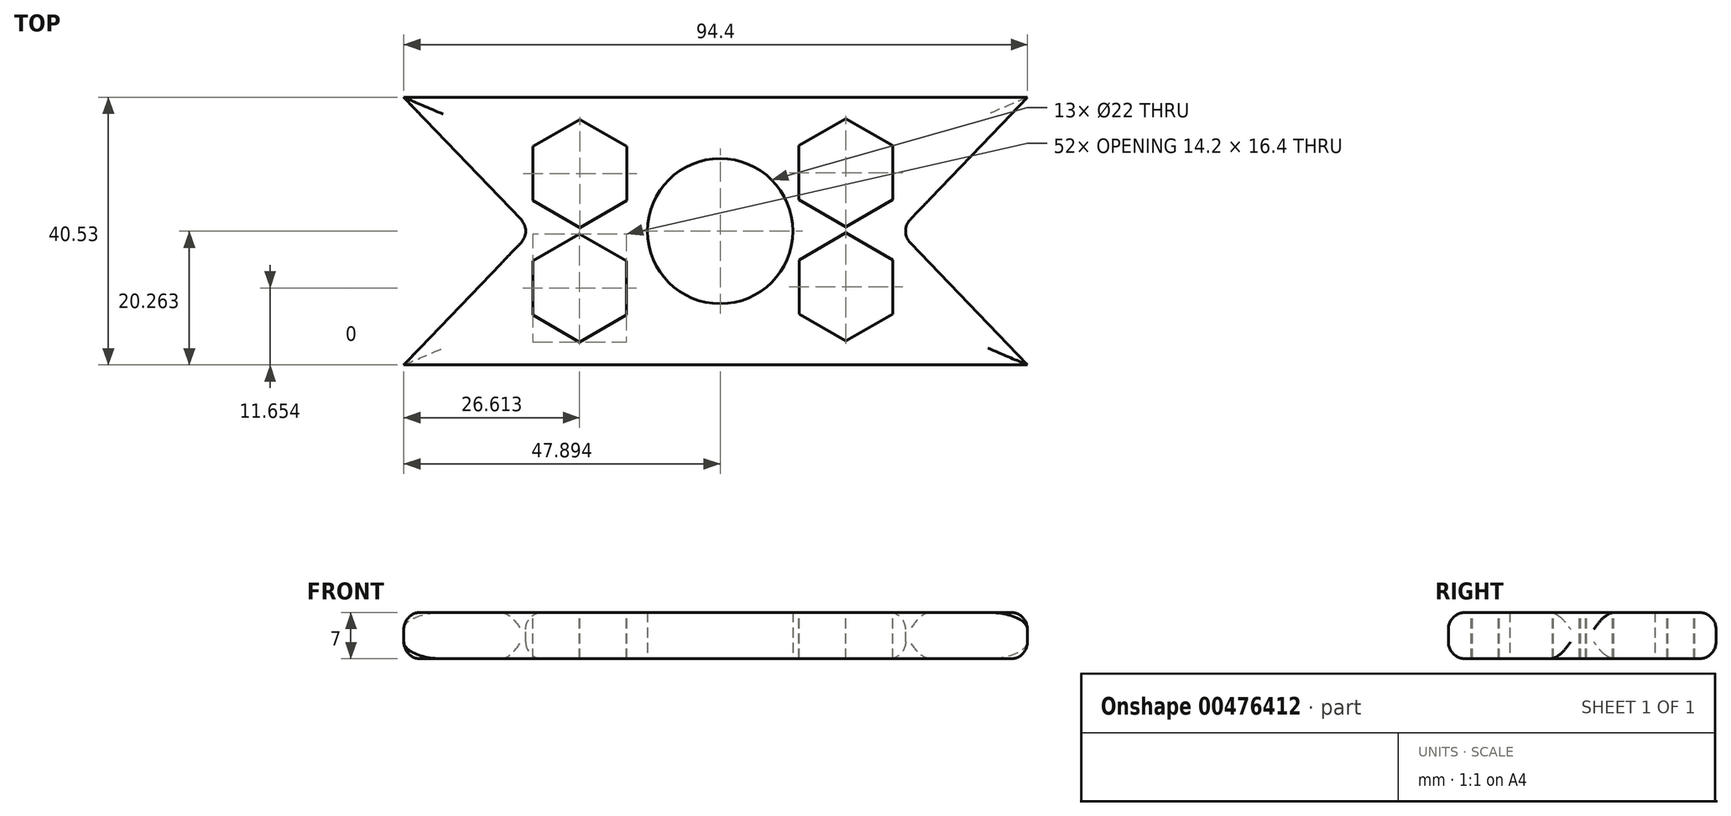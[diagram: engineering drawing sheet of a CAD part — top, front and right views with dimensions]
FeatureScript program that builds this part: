
annotation { "Feature Type Name" : "Feature", "Feature Type Description" : "" }
export const myFeature = defineFeature(function(context is Context, id is Id, definition is map)
    precondition{}
    {
        {
            var Q0;
            Q0=qCreatedBy(makeId("Top.planeOp"),FACE);
            var sketch = newSketch(context, id + "F0", { "sketchPlane" : qUnion([Q0])});
            skLineSegment(sketch, "E0", {"start": v(1.37, -16.47) * mm, "end": v(-46.52, -16.47) * mm});
            skLineSegment(sketch, "E1", {"start": v(-46.52, 24.06) * mm, "end": v(1.37, 24.06) * mm});
            skLineSegment(sketch, "E2", {"start": v(1.37, 24.06) * mm, "end": v(47.88, 24.06) * mm});
            skLineSegment(sketch, "E3", {"start": v(1.37, -16.47) * mm, "end": v(47.88, -16.47) * mm});
            skCircle(sketch, "E4", {"center": v(1.37, 3.8) * mm, "radius": 11 * mm});
            skLineSegment(sketch, "E5", {"start": v(-46.52, 24.06) * mm, "end": v(-27.1, 3.8) * mm});
            skLineSegment(sketch, "E6", {"start": v(-27.1, 3.8) * mm, "end": v(-46.52, -16.47) * mm});
            skLineSegment(sketch, "E7", {"start": v(47.88, 24.06) * mm, "end": v(28.47, 3.8) * mm});
            skLineSegment(sketch, "E8", {"start": v(28.47, 3.8) * mm, "end": v(47.88, -16.47) * mm});
            skArc(sketch, "E9", {"start": v(-36.8, 13.92) * mm, "mid": v(-38.9, 3.8) * mm, "end": v(-36.8, -6.34) * mm});
            skArc(sketch, "E10", {"start": v(38.18, -6.34) * mm, "mid": v(40.27, 3.8) * mm, "end": v(38.18, 13.92) * mm});
            skSolve(sketch);
        }
        {
            var Q0;
            Q0=makeQuery(id+"F0.imprint","IMPRINT",FACE,{"disambiguationData":[TD([[makeQuery(id+"F0.imprint","IMPRINT",EDGE,{"derivedFrom":sQuery(id+"F0.wireOp",EDGE,"E0")}),-1.0]])]});
            extrude(context, id + "F1", {"entities" : qUnion([Q0]), "depth" : 7 * mm});
        }
        {
            var Q0;
            Q0=makeQuery(id+"F1.opExtrude","CAP_EDGE",EDGE,{"disambiguationData":[OSD([sQuery(id+"F0.wireOp",EDGE,"E0"),sQuery(id+"F0.wireOp",EDGE,"E3")])],"isStart":false});
            var Q1;
            Q1=makeQuery(id+"F1.opExtrude","CAP_EDGE",EDGE,{"disambiguationData":[OSD([sQuery(id+"F0.wireOp",EDGE,"E1"),sQuery(id+"F0.wireOp",EDGE,"E2")])],"isStart":false});
            var Q2;
            Q2=makeQuery(id+"F1.opExtrude","CAP_EDGE",EDGE,{"disambiguationData":[OSD([sQuery(id+"F0.wireOp",EDGE,"E1"),sQuery(id+"F0.wireOp",EDGE,"E2")])],"isStart":true});
            var Q3;
            Q3=makeQuery(id+"F1.opExtrude","CAP_EDGE",EDGE,{"disambiguationData":[OSD([sQuery(id+"F0.wireOp",EDGE,"E0"),sQuery(id+"F0.wireOp",EDGE,"E3")])],"isStart":true});
            var Q4;
            Q4=makeQuery(id+"F1.opExtrude","SWEPT_EDGE",EDGE,{"disambiguationData":[OSD([sQuery(id+"F0.wireOp",EDGE,"E7"),sQuery(id+"F0.wireOp",EDGE,"E8")])]});
            var Q5;
            Q5=makeQuery(id+"F1.opExtrude","SWEPT_EDGE",EDGE,{"disambiguationData":[OSD([sQuery(id+"F0.wireOp",EDGE,"E5"),sQuery(id+"F0.wireOp",EDGE,"E6")])]});
            var Q6;
            Q6=makeQuery(id+"F1.opExtrude","CAP_EDGE",EDGE,{"disambiguationData":[OSD([sQuery(id+"F0.wireOp",EDGE,"E8")])],"isStart":false});
            var Q7;
            Q7=makeQuery(id+"F1.opExtrude","CAP_EDGE",EDGE,{"disambiguationData":[OSD([sQuery(id+"F0.wireOp",EDGE,"E5")])],"isStart":false});
            var Q8;
            Q8=makeQuery(id+"F1.opExtrude","CAP_EDGE",EDGE,{"disambiguationData":[OSD([sQuery(id+"F0.wireOp",EDGE,"E6")])],"isStart":true});
            var Q9;
            Q9=makeQuery(id+"F1.opExtrude","CAP_EDGE",EDGE,{"disambiguationData":[OSD([sQuery(id+"F0.wireOp",EDGE,"E7")])],"isStart":true});
            fillet(context, id + "F2", {"entities" : qUnion([Q0, Q1, Q2, Q3, Q4, Q5, Q6, Q7, Q8, Q9]), "radius" : 2.54 * mm, "tangentPropagation" : true, "allowEdgeOverflow" : false});
        }
        {
            var Q0;
            Q0=makeQuery(id+"F1.opExtrude","CAP_FACE",FACE,{"disambiguationData":[OSD([sQuery(id+"F0.wireOp",EDGE,"E0"),sQuery(id+"F0.wireOp",EDGE,"E1"),sQuery(id+"F0.wireOp",EDGE,"E2"),sQuery(id+"F0.wireOp",EDGE,"E3"),sQuery(id+"F0.wireOp",EDGE,"E4"),sQuery(id+"F0.wireOp",EDGE,"E5"),sQuery(id+"F0.wireOp",EDGE,"E6"),sQuery(id+"F0.wireOp",EDGE,"E7"),sQuery(id+"F0.wireOp",EDGE,"E8")])],"isStart":false});
            var sketch = newSketch(context, id + "F3", { "sketchPlane" : qUnion([Q0])});
            skPoint(sketch, "E11.0.midPoint", {"position": v(-8.39, 9.42) * mm});
            skLineSegment(sketch, "E12.0", {"start": v(-12.75, 16.6) * mm, "end": v(-12.75, 8.4) * mm});
            skLineSegment(sketch, "E12.1", {"start": v(-12.75, 8.4) * mm, "end": v(-19.85, 4.3) * mm});
            skLineSegment(sketch, "E12.2", {"start": v(-19.85, 4.3) * mm, "end": v(-26.95, 8.4) * mm});
            skLineSegment(sketch, "E12.3", {"start": v(-26.95, 8.4) * mm, "end": v(-26.95, 16.6) * mm});
            skLineSegment(sketch, "E12.4", {"start": v(-26.95, 16.6) * mm, "end": v(-19.85, 20.7) * mm});
            skLineSegment(sketch, "E12.5", {"start": v(-19.85, 20.7) * mm, "end": v(-12.75, 16.6) * mm});
            skPoint(sketch, "E12.0.midPoint", {"position": v(-17.2, 13.9) * mm});
            skPoint(sketch, "E13.0.midPoint", {"position": v(-11.71, -9.21) * mm});
            skSolve(sketch);
        }
        {
            var Q0;
            Q0=makeQuery(id+"F3.imprint","IMPRINT",FACE,{"disambiguationData":[TD([[makeQuery(id+"F3.imprint","IMPRINT",EDGE,{"derivedFrom":sQuery(id+"F3.wireOp",EDGE,"E12.0")}),1.0]])]});
            var sketch = newSketch(context, id + "F4", { "sketchPlane" : qUnion([Q0])});
            skLineSegment(sketch, "E14.0", {"start": v(-12.8, -0.72) * mm, "end": v(-12.8, -8.92) * mm});
            skLineSegment(sketch, "E14.1", {"start": v(-12.8, -8.92) * mm, "end": v(-19.9, -13.01) * mm});
            skLineSegment(sketch, "E14.2", {"start": v(-19.9, -13.01) * mm, "end": v(-27, -8.92) * mm});
            skLineSegment(sketch, "E14.3", {"start": v(-27, -8.92) * mm, "end": v(-27, -0.72) * mm});
            skLineSegment(sketch, "E14.4", {"start": v(-27, -0.72) * mm, "end": v(-19.9, 3.38) * mm});
            skLineSegment(sketch, "E14.5", {"start": v(-19.9, 3.38) * mm, "end": v(-12.8, -0.72) * mm});
            skPoint(sketch, "E14.0.midPoint", {"position": v(-14, -7.22) * mm});
            skSolve(sketch);
        }
        {
            var Q0;
            Q0=makeQuery(id+"F3.imprint","IMPRINT",FACE,{"disambiguationData":[TD([[makeQuery(id+"F3.imprint","IMPRINT",EDGE,{"derivedFrom":sQuery(id+"F3.wireOp",EDGE,"E12.0")}),1.0]])]});
            var sketch = newSketch(context, id + "F5", { "sketchPlane" : qUnion([Q0])});
            skLineSegment(sketch, "E15.0", {"start": v(27.5, 16.74) * mm, "end": v(27.5, 8.54) * mm});
            skLineSegment(sketch, "E15.1", {"start": v(27.5, 8.54) * mm, "end": v(20.4, 4.44) * mm});
            skLineSegment(sketch, "E15.2", {"start": v(20.4, 4.44) * mm, "end": v(13.3, 8.54) * mm});
            skLineSegment(sketch, "E15.3", {"start": v(13.3, 8.54) * mm, "end": v(13.3, 16.74) * mm});
            skLineSegment(sketch, "E15.4", {"start": v(13.3, 16.74) * mm, "end": v(20.4, 20.84) * mm});
            skLineSegment(sketch, "E15.5", {"start": v(20.4, 20.84) * mm, "end": v(27.5, 16.74) * mm});
            skPoint(sketch, "E15.0.midPoint", {"position": v(27.5, 12.74) * mm});
            skSolve(sketch);
        }
        {
            var Q0;
            Q0=makeQuery(id+"F3.imprint","IMPRINT",FACE,{"disambiguationData":[TD([[makeQuery(id+"F3.imprint","IMPRINT",EDGE,{"derivedFrom":sQuery(id+"F3.wireOp",EDGE,"E12.0")}),1.0]])]});
            var sketch = newSketch(context, id + "F6", { "sketchPlane" : qUnion([Q0])});
            skLineSegment(sketch, "E16.0", {"start": v(27.52, -0.55) * mm, "end": v(27.52, -8.75) * mm});
            skLineSegment(sketch, "E16.1", {"start": v(27.52, -8.75) * mm, "end": v(20.42, -12.85) * mm});
            skLineSegment(sketch, "E16.2", {"start": v(20.42, -12.85) * mm, "end": v(13.32, -8.75) * mm});
            skLineSegment(sketch, "E16.3", {"start": v(13.32, -8.75) * mm, "end": v(13.32, -0.55) * mm});
            skLineSegment(sketch, "E16.4", {"start": v(13.32, -0.55) * mm, "end": v(20.42, 3.55) * mm});
            skLineSegment(sketch, "E16.5", {"start": v(20.42, 3.55) * mm, "end": v(27.52, -0.55) * mm});
            skPoint(sketch, "E16.0.midPoint", {"position": v(25.62, -8.15) * mm});
            skSolve(sketch);
        }
        {
            var Q0;
            Q0=makeQuery(id+"F3.imprint","IMPRINT",FACE,{"disambiguationData":[TD([[makeQuery(id+"F3.imprint","IMPRINT",EDGE,{"derivedFrom":sQuery(id+"F3.wireOp",EDGE,"E12.0")}),-1.0]])]});
            extrude(context, id + "F7", {"entities" : qUnion([Q0]), "operationType" : NewBodyOperationType.REMOVE, "endBound" : BoundingType.THROUGH_ALL, "oppositeDirection" : true, "depth" : 25 * mm});
        }
        {
            var Q0;
            Q0=makeQuery(id+"F4.imprint","IMPRINT",FACE,{"disambiguationData":[TD([[makeQuery(id+"F4.imprint","IMPRINT",EDGE,{"derivedFrom":sQuery(id+"F4.wireOp",EDGE,"E14.0")}),-1.0]])]});
            extrude(context, id + "F8", {"entities" : qUnion([Q0]), "operationType" : NewBodyOperationType.REMOVE, "endBound" : BoundingType.THROUGH_ALL, "oppositeDirection" : true, "depth" : 25 * mm});
        }
        {
            var Q0;
            Q0=makeQuery(id+"F6.imprint","IMPRINT",FACE,{"disambiguationData":[TD([[makeQuery(id+"F6.imprint","IMPRINT",EDGE,{"derivedFrom":sQuery(id+"F6.wireOp",EDGE,"E16.0")}),-1.0]])]});
            extrude(context, id + "F9", {"entities" : qUnion([Q0]), "operationType" : NewBodyOperationType.REMOVE, "endBound" : BoundingType.THROUGH_ALL, "oppositeDirection" : true, "depth" : 25 * mm});
        }
        {
            var Q0;
            Q0=makeQuery(id+"F5.imprint","IMPRINT",FACE,{"disambiguationData":[TD([[makeQuery(id+"F5.imprint","IMPRINT",EDGE,{"derivedFrom":sQuery(id+"F5.wireOp",EDGE,"E15.0")}),-1.0]])]});
            extrude(context, id + "F10", {"entities" : qUnion([Q0]), "operationType" : NewBodyOperationType.REMOVE, "endBound" : BoundingType.THROUGH_ALL, "oppositeDirection" : true, "depth" : 25 * mm});
        }
    });
